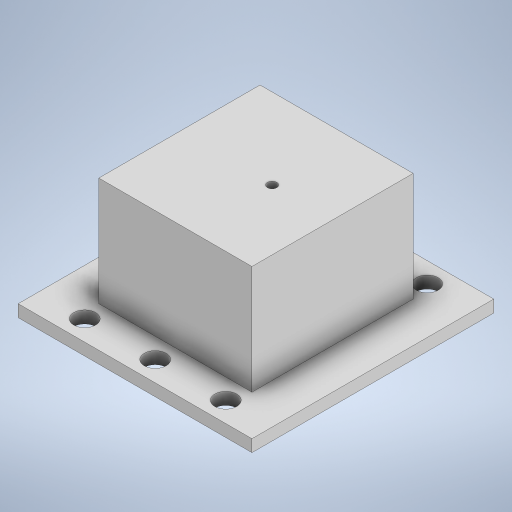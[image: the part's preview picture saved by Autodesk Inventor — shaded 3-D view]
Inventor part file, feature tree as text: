
AUTODESK INVENTOR PART (.ipt)
format: ipt  version: 2024 (Build 280153000, 153)  size: 320,000 bytes
history: native  units: mm
features: extrude x7, sketch x7, plane x3
ambient origin geometry x8: Origin, YZ Plane, XZ Plane, XY Plane, X Axis, Y Axis, Z Axis, Center Point
bodies: Body1 (feature_tree)
feature tree (17):
  plane  "Work Plane5"
  extrude  "Extrusion34"  Depth=40.0mm
  plane  "Work Plane2"
  extrude  "Extrusion35"  Depth=30.0mm
  plane  "Work Plane1"
  extrude  "Extrusion51"  Depth=30.0mm
  sketch  "Sketch77"  dims[d211=10.0mm d212=0.0mm d219=35.0mm]
  extrude  "Extrusion53"  Depth=10.0mm
  extrude  "Extrusion54"  Depth=60.0mm
  extrude  "Extrusion56"  Depth=3.0mm TaperAngle=0.0deg
  extrude  "Extrusion57"  Depth=4.5mm
  sketch  "Sketch45"  dims[d142=38.0mm d143=40.0mm]
  sketch  "Sketch47"  dims[d144=30.0mm d145=0.0mm d146=36.0mm]
  sketch  "Sketch74"  dims[d147=30.0mm d148=-2.617994mm d210=2.3mm]
  sketch  "Sketch78"  dims[d220=58.0mm d221=60.0mm]
  sketch  "Sketch81"  dims[d222=3.0mm d223=0.0mm d224=3.0mm d225=0.0mm]
  sketch  "Sketch83"  dims[d232=5.0mm d233=11.5mm d234=5.4mm d235=17.5mm d236=5.4mm d237=17.5mm d238=5.4mm d239=5.0mm d240=17.0mm d241=5.4mm d242=16.0mm d243=5.4mm d244=17.0mm d245=5.4mm d246=17.5mm d247=5.4mm d248=17.5mm d249=5.0mm d250=30.0mm d251=0.0mm d253=4.8mm d254=4.5mm d255=0.0mm d49=0.5mm d50=0.872665mm d51=0.5mm d52=0.872665mm d130=0.5mm d131=0.872665mm d132=0.5mm d133=0.872665mm d156=0.5mm d157=0.872665mm d158=0.5mm d159=0.872665mm d173=0.5mm d174=0.872665mm d175=0.5mm d176=0.872665mm d226=0.5mm d227=0.872665mm]
